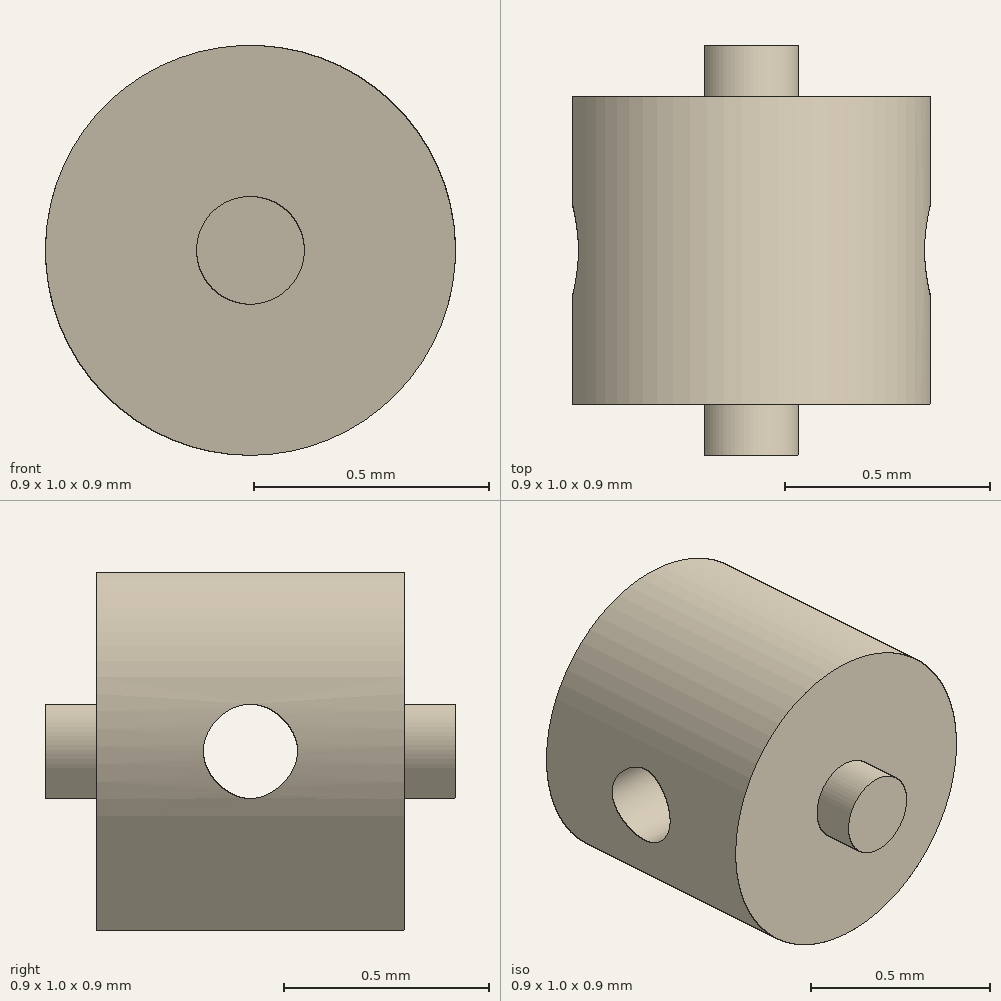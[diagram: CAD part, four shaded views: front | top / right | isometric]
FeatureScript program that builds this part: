
annotation { "Feature Type Name" : "Feature", "Feature Type Description" : "" }
export const myFeature = defineFeature(function(context is Context, id is Id, definition is map)
    precondition{}
    {
        {
            var Q0;
            Q0=qCreatedBy(makeId("Front.planeOp"),FACE);
            var sketch = newSketch(context, id + "F0", { "sketchPlane" : qUnion([Q0])});
            skCircle(sketch, "E0", {"center": v(0, 0) * mm, "radius": 0.12 * mm});
            skCircle(sketch, "E1", {"center": v(0, 0) * mm, "radius": 0.44 * mm});
            skSolve(sketch);
        }
        {
            var Q0;
            Q0=makeQuery(id+"F0.imprint","IMPRINT",FACE,{"disambiguationData":[TD([[makeQuery(id+"F0.imprint","IMPRINT",EDGE,{"derivedFrom":sQuery(id+"F0.wireOp",EDGE,"E0")}),-1.0]])]});
            extrude(context, id + "F1", {"entities" : qUnion([Q0]), "depth" : 0.75 * mm, "offsetDistance" : 25 * mm});
        }
        {
            var Q0;
            Q0=makeQuery(id+"F0.imprint","IMPRINT",FACE,{"disambiguationData":[TD([[makeQuery(id+"F0.imprint","IMPRINT",EDGE,{"derivedFrom":sQuery(id+"F0.wireOp",EDGE,"E0")}),1.0]])]});
            extrude(context, id + "F2", {"entities" : qUnion([Q0]), "operationType" : NewBodyOperationType.ADD, "depth" : 0.88 * mm, "offsetDistance" : 25 * mm, "hasSecondDirection" : true, "secondDirectionOppositeDirection" : true, "secondDirectionDepth" : 0.12 * mm});
        }
        {
            var Q0;
            Q0=qCreatedBy(makeId("Right.planeOp"),FACE);
            var sketch = newSketch(context, id + "F3", { "sketchPlane" : qUnion([Q0])});
            skCircle(sketch, "E2", {"center": v(-0.38, 0) * mm, "radius": 0.12 * mm});
            skSolve(sketch);
        }
        {
            var Q0;
            Q0=qSketchRegion(id+"F3",true);
            extrude(context, id + "F4", {"entities" : qUnion([Q0]), "operationType" : NewBodyOperationType.REMOVE, "depth" : 25 * mm, "offsetDistance" : 25 * mm, "hasSecondDirection" : true, "secondDirectionOppositeDirection" : true, "secondDirectionDepth" : 25 * mm});
        }
    });
